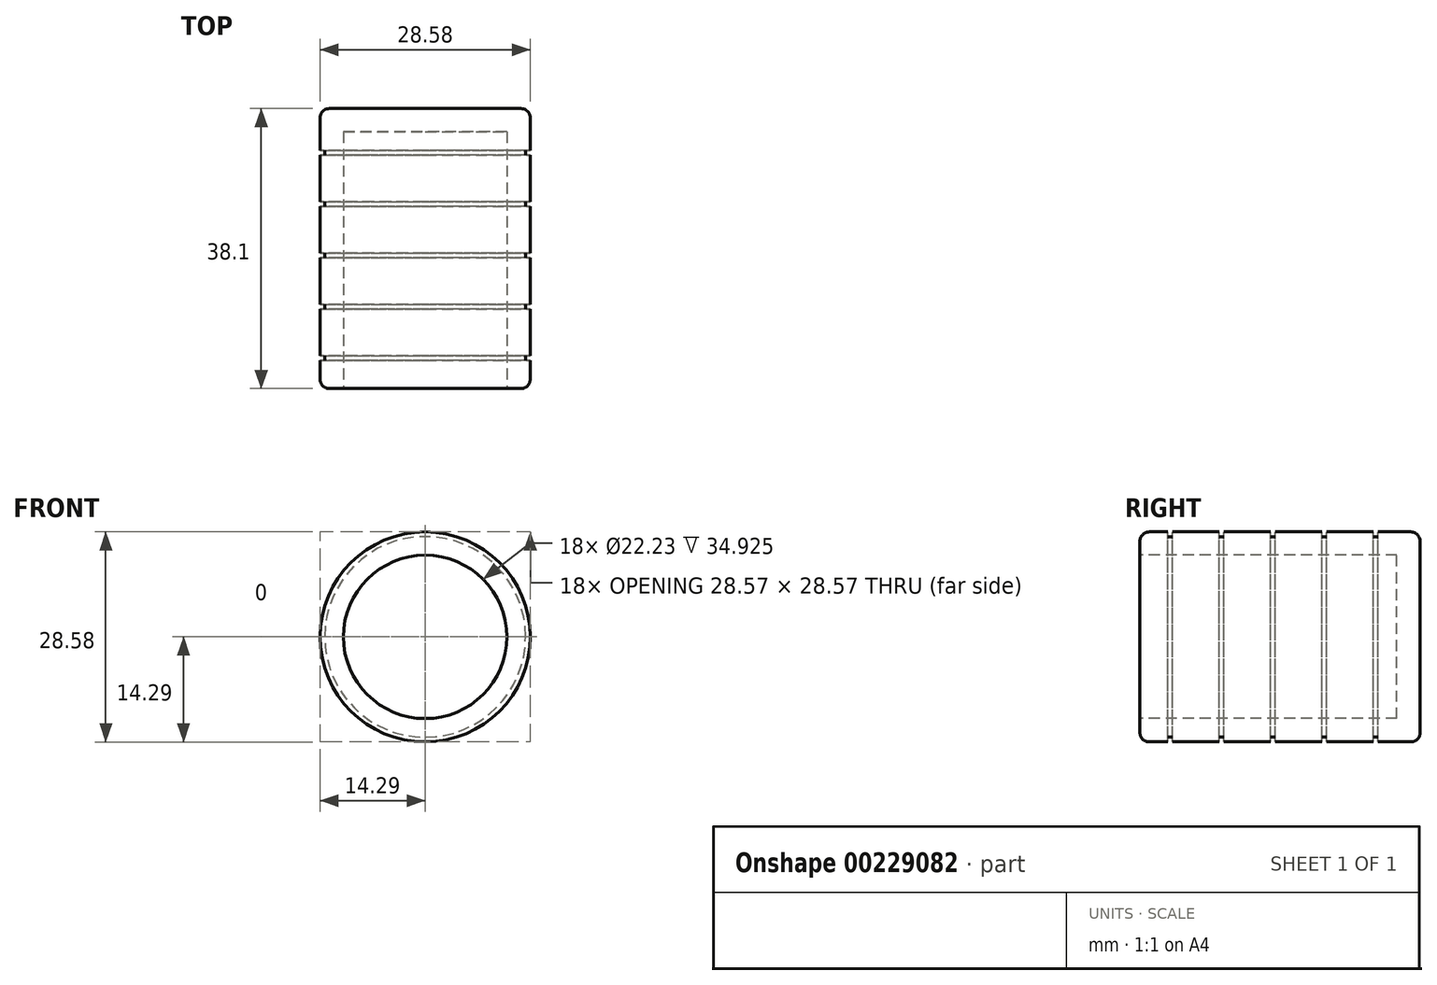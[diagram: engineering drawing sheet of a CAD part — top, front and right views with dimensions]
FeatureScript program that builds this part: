
annotation { "Feature Type Name" : "Feature", "Feature Type Description" : "" }
export const myFeature = defineFeature(function(context is Context, id is Id, definition is map)
    precondition{}
    {
        {
            var Q0;
            Q0=qCreatedBy(makeId("Front.planeOp"),FACE);
            var sketch = newSketch(context, id + "F0", { "sketchPlane" : qUnion([Q0])});
            skCircle(sketch, "E0", {"center": v(0, 0) * mm, "radius": 14.29 * mm});
            skSolve(sketch);
        }
        {
            var Q0;
            Q0 = qSketchRegion(id + "F0", true);
            extrude(context, id + "F1", {"entities" : qUnion([Q0]), "depth" : 38.1 * mm});
        }
        {
            var Q0;
            Q0=makeQuery(id+"F1.opExtrude","CAP_FACE",FACE,{"disambiguationData":[OSD([sQuery(id+"F0.wireOp",EDGE,"E0")])],"isStart":false});
            var sketch = newSketch(context, id + "F2", { "sketchPlane" : qUnion([Q0])});
            skCircle(sketch, "E1", {"center": v(0, 0) * mm, "radius": 11.11 * mm});
            skSolve(sketch);
        }
        {
            var Q0;
            Q0 = qSketchRegion(id + "F2", true);
            extrude(context, id + "F3", {"entities" : qUnion([Q0]), "operationType" : NewBodyOperationType.REMOVE, "oppositeDirection" : true, "depth" : 34.92 * mm});
        }
        {
            var Q0;
            Q0=makeQuery(id+"F1.opExtrude","CAP_EDGE",EDGE,{"disambiguationData":[OSD([sQuery(id+"F0.wireOp",EDGE,"E0")])],"isStart":true});
            var Q1;
            Q1=makeQuery(id+"F1.opExtrude","CAP_EDGE",EDGE,{"disambiguationData":[OSD([sQuery(id+"F0.wireOp",EDGE,"E0")])],"isStart":false});
            fillet(context, id + "F4", {"entities" : qUnion([Q0, Q1]), "radius" : 1.27 * mm, "tangentPropagation" : true, "allowEdgeOverflow" : false});
        }
        {
            var Q0;
            Q0=qCreatedBy(makeId("Right.planeOp"),FACE);
            var sketch = newSketch(context, id + "F5", { "sketchPlane" : qUnion([Q0])});
            skLineSegment(sketch, "E2", {"start": v(-6.35, 14.28) * mm, "end": v(-6.35, 13.65) * mm});
            skLineSegment(sketch, "E3", {"start": v(-5.72, 13.65) * mm, "end": v(-6.35, 13.65) * mm});
            skLineSegment(sketch, "E4", {"start": v(-5.72, 13.65) * mm, "end": v(-5.72, 14.28) * mm});
            skLineSegment(sketch, "E5", {"start": v(-12.7, 14.28) * mm, "end": v(-13.34, 14.28) * mm});
            skLineSegment(sketch, "E6", {"start": v(-13.34, 14.28) * mm, "end": v(-13.34, 13.65) * mm});
            skLineSegment(sketch, "E7", {"start": v(-12.7, 13.65) * mm, "end": v(-13.34, 13.65) * mm});
            skLineSegment(sketch, "E8", {"start": v(-12.7, 13.65) * mm, "end": v(-12.7, 14.28) * mm});
            skLineSegment(sketch, "E9", {"start": v(-19.69, 14.28) * mm, "end": v(-19.69, 13.65) * mm});
            skLineSegment(sketch, "E10", {"start": v(-19.69, 13.65) * mm, "end": v(-20.32, 13.65) * mm});
            skLineSegment(sketch, "E11", {"start": v(-20.32, 13.65) * mm, "end": v(-20.32, 14.28) * mm});
            skLineSegment(sketch, "E12", {"start": v(-26.67, 14.28) * mm, "end": v(-26.67, 13.65) * mm});
            skLineSegment(sketch, "E13", {"start": v(-26.67, 13.65) * mm, "end": v(-27.3, 13.65) * mm});
            skLineSegment(sketch, "E14", {"start": v(-27.3, 13.65) * mm, "end": v(-27.3, 14.28) * mm});
            skLineSegment(sketch, "E15", {"start": v(-33.66, 14.28) * mm, "end": v(-33.66, 13.65) * mm});
            skLineSegment(sketch, "E16", {"start": v(-33.66, 13.65) * mm, "end": v(-34.3, 13.65) * mm});
            skLineSegment(sketch, "E17", {"start": v(-34.3, 13.65) * mm, "end": v(-34.3, 14.28) * mm});
            skLineSegment(sketch, "E18", {"start": v(-5.72, 14.28) * mm, "end": v(-6.35, 14.28) * mm});
            skLineSegment(sketch, "E19", {"start": v(-26.67, 14.28) * mm, "end": v(-27.3, 14.28) * mm});
            skLineSegment(sketch, "E20", {"start": v(-33.66, 14.28) * mm, "end": v(-34.3, 14.28) * mm});
            skLineSegment(sketch, "E21", {"start": v(-19.69, 14.28) * mm, "end": v(-20.32, 14.28) * mm});
            skLineSegment(sketch, "E22", {"start": v(0, 0) * mm, "end": v(-42.47, 0) * mm});
            skSolve(sketch);
        }
        {
            var Q0;
            Q0 = qSketchRegion(id + "F5", true);
            var Q1;
            Q1=sQuery(id+"F5.wireOp",EDGE,"E22");
            revolve(context, id + "F6", {"operationType" : NewBodyOperationType.REMOVE, "entities" : qUnion([Q0]), "axis" : qUnion([Q1]), "revolveType" : RevolveType.FULL, "oppositeDirection" : true});
        }
    });
